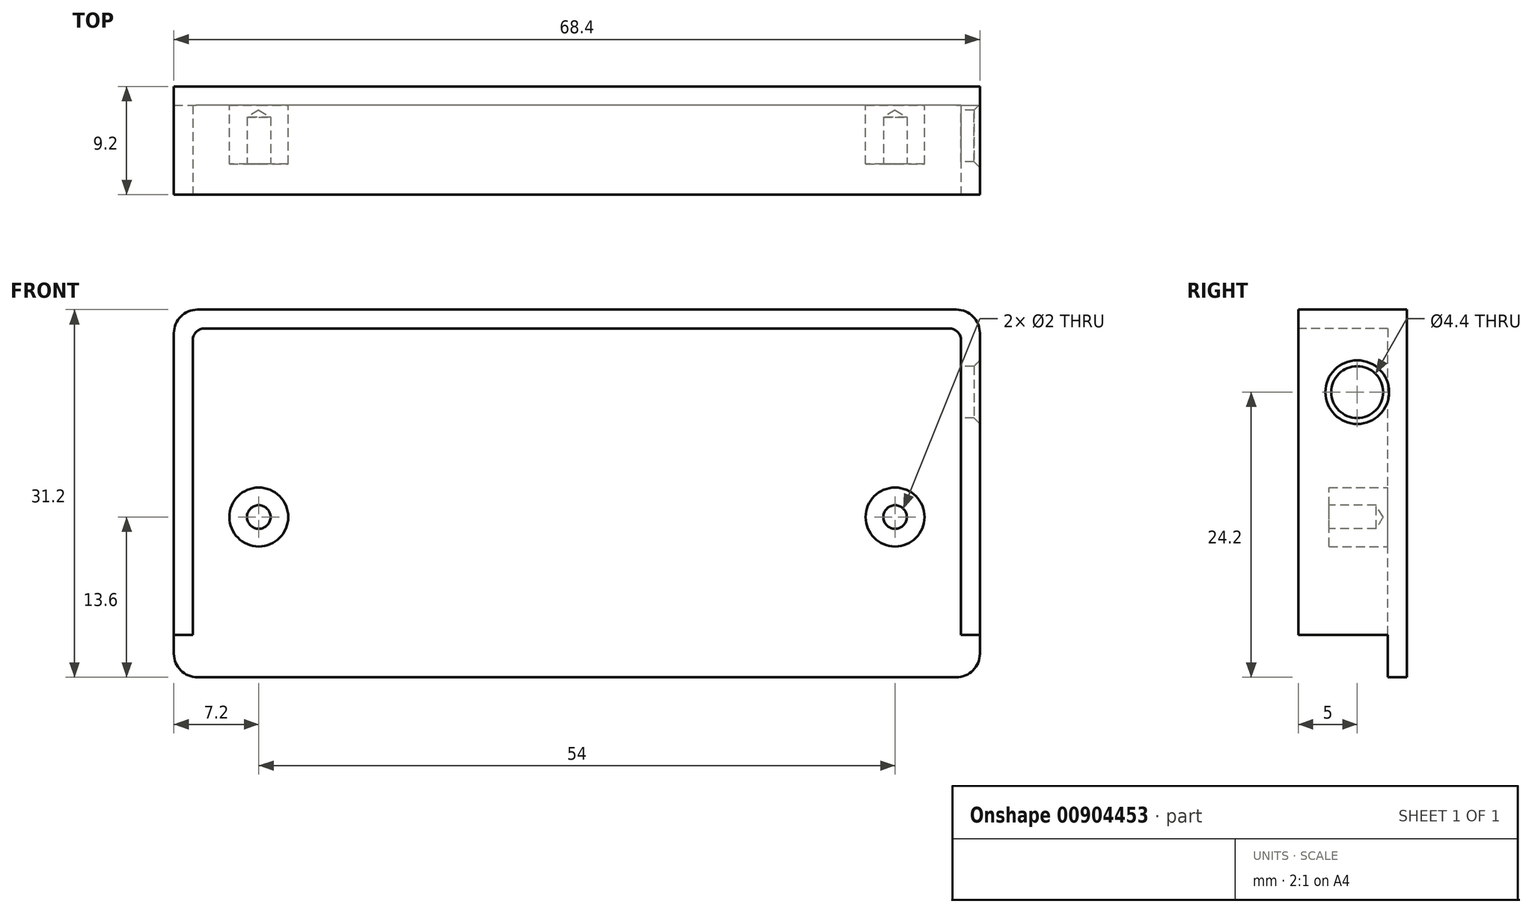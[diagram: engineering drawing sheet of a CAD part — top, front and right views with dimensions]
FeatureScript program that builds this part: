
annotation { "Feature Type Name" : "Feature", "Feature Type Description" : "" }
export const myFeature = defineFeature(function(context is Context, id is Id, definition is map)
    precondition{}
    {
        {
            var Q0;
            Q0=qCreatedBy(makeId("Front.planeOp"),FACE);
            var sketch = newSketch(context, id + "F0", { "sketchPlane" : qUnion([Q0])});
            skLineSegment(sketch, "E0.bottom", {"start": v(34.2, -15.6) * mm, "end": v(-34.2, -15.6) * mm});
            skLineSegment(sketch, "E0.top", {"start": v(34.2, 15.6) * mm, "end": v(-34.2, 15.6) * mm});
            skLineSegment(sketch, "E0.left", {"start": v(34.2, -15.6) * mm, "end": v(34.2, 15.6) * mm});
            skLineSegment(sketch, "E0.right", {"start": v(-34.2, -15.6) * mm, "end": v(-34.2, 15.6) * mm});
            skPoint(sketch, "E0.middle", {"position": v(0, 0) * mm});
            skSolve(sketch);
        }
        {
            var Q0;
            Q0=qSketchRegion(id+"F0",true);
            extrude(context, id + "F1", {"entities" : qUnion([Q0]), "depth" : 9.2 * mm, "offsetDistance" : 25 * mm});
        }
        {
            var Q0;
            Q0=makeQuery(id+"F1.opExtrude","CAP_FACE",FACE,{"disambiguationData":[OSD([sQuery(id+"F0.wireOp",EDGE,"E0.bottom"),sQuery(id+"F0.wireOp",EDGE,"E0.top"),sQuery(id+"F0.wireOp",EDGE,"E0.left"),sQuery(id+"F0.wireOp",EDGE,"E0.right")])],"isStart":false});
            var sketch = newSketch(context, id + "F2", { "sketchPlane" : qUnion([Q0])});
            skLineSegment(sketch, "E1.top", {"start": v(31.6, 14) * mm, "end": v(-31.6, 14) * mm});
            skLineSegment(sketch, "E1.left", {"start": v(32.6, -12) * mm, "end": v(32.6, 13) * mm});
            skLineSegment(sketch, "E1.right", {"start": v(-32.6, -12) * mm, "end": v(-32.6, 13) * mm});
            skPoint(sketch, "E1.middle", {"position": v(0, 1) * mm});
            skCircle(sketch, "E2", {"center": v(-31.6, 13) * mm, "radius": 1 * mm});
            skPoint(sketch, "E2.first.point", {"position": v(-32.6, 13) * mm});
            skPoint(sketch, "E2.second.point", {"position": v(-31.6, 14) * mm});
            skPoint(sketch, "E2.third.point", {"position": v(-30.68, 12.62) * mm});
            skCircle(sketch, "E3", {"center": v(31.6, 13) * mm, "radius": 1 * mm});
            skPoint(sketch, "E3.first.point", {"position": v(32.6, 13) * mm});
            skPoint(sketch, "E3.second.point", {"position": v(31.6, 14) * mm});
            skPoint(sketch, "E3.third.point", {"position": v(30.96, 12.23) * mm});
            skPoint(sketch, "E4.orphan", {"position": v(-32.6, 14) * mm});
            skPoint(sketch, "E5.orphan", {"position": v(32.6, 14) * mm});
            skLineSegment(sketch, "E6.bottom", {"start": v(-34.2, -12) * mm, "end": v(-32.6, -12) * mm});
            skLineSegment(sketch, "E6.top", {"start": v(-34.2, -15.6) * mm, "end": v(34.2, -15.6) * mm});
            skLineSegment(sketch, "E6.left", {"start": v(-34.2, -12) * mm, "end": v(-34.2, -15.6) * mm});
            skLineSegment(sketch, "E6.right", {"start": v(34.2, -12) * mm, "end": v(34.2, -15.6) * mm});
            skLineSegment(sketch, "E7.trimOffspring", {"start": v(32.6, -12) * mm, "end": v(34.2, -12) * mm});
            skSolve(sketch);
        }
        {
            var Q0;
            Q0=qSketchRegion(id+"F2",true);
            extrude(context, id + "F3", {"entities" : qUnion([Q0]), "operationType" : NewBodyOperationType.REMOVE, "oppositeDirection" : true, "depth" : 7.6 * mm, "offsetDistance" : 25 * mm});
        }
        {
            var Q0;
            Q0=makeQuery(id+"F1.opExtrude","SWEPT_EDGE",EDGE,{"disambiguationData":[OSD([sQuery(id+"F0.wireOp",EDGE,"E0.top"),sQuery(id+"F0.wireOp",EDGE,"E0.left")])]});
            fillet(context, id + "F4", {"entities" : qUnion([Q0]), "radius" : 2 * mm, "tangentPropagation" : true, "allowEdgeOverflow" : false});
        }
        {
            var Q0;
            Q0=makeQuery(id+"F1.opExtrude","SWEPT_EDGE",EDGE,{"disambiguationData":[OSD([sQuery(id+"F0.wireOp",EDGE,"E0.top"),sQuery(id+"F0.wireOp",EDGE,"E0.right")])]});
            var Q1;
            Q1=makeQuery(id+"F1.opExtrude","SWEPT_EDGE",EDGE,{"disambiguationData":[OSD([sQuery(id+"F0.wireOp",EDGE,"E0.bottom"),sQuery(id+"F0.wireOp",EDGE,"E0.right")])]});
            fillet(context, id + "F5", {"entities" : qUnion([Q0, Q1]), "radius" : 2 * mm, "tangentPropagation" : true, "allowEdgeOverflow" : false});
        }
        {
            var Q0;
            Q0=makeQuery(id+"F1.opExtrude","SWEPT_EDGE",EDGE,{"disambiguationData":[OSD([sQuery(id+"F0.wireOp",EDGE,"E0.bottom"),sQuery(id+"F0.wireOp",EDGE,"E0.left")])]});
            fillet(context, id + "F6", {"entities" : qUnion([Q0]), "radius" : 2 * mm, "tangentPropagation" : true, "allowEdgeOverflow" : false});
        }
        {
            var Q0;
            Q0=makeQuery(id+"F3.boolean.opBoolean","COPY",FACE,{"derivedFrom":makeQuery(id+"F3.opExtrude","CAP_FACE",FACE,{"disambiguationData":[OSD([sQuery(id+"F2.wireOp",EDGE,"E1.top"),sQuery(id+"F2.wireOp",EDGE,"E1.left"),sQuery(id+"F2.wireOp",EDGE,"E1.right"),sQuery(id+"F2.wireOp",EDGE,"E2"),sQuery(id+"F2.wireOp",EDGE,"E3"),sQuery(id+"F2.wireOp",EDGE,"E6.bottom"),sQuery(id+"F2.wireOp",EDGE,"E6.top"),sQuery(id+"F2.wireOp",EDGE,"E6.left"),sQuery(id+"F2.wireOp",EDGE,"E6.right"),sQuery(id+"F2.wireOp",EDGE,"E7.trimOffspring")])],"isStart":false})});
            var sketch = newSketch(context, id + "F7", { "sketchPlane" : qUnion([Q0])});
            skCircle(sketch, "E8", {"center": v(-27, -2) * mm, "radius": 2.5 * mm});
            skPoint(sketch, "E8.first.point", {"position": v(-29.27, -3.04) * mm});
            skPoint(sketch, "E8.second.point", {"position": v(-26.63, -4.47) * mm});
            skPoint(sketch, "E8.third.point", {"position": v(-27.02, 0.5) * mm});
            skCircle(sketch, "E9", {"center": v(27, -2) * mm, "radius": 2.5 * mm});
            skPoint(sketch, "E9.first.point", {"position": v(26.98, 0.5) * mm});
            skPoint(sketch, "E9.second.point", {"position": v(29.46, -1.55) * mm});
            skPoint(sketch, "E9.third.point", {"position": v(27.02, 0.5) * mm});
            skSolve(sketch);
        }
        {
            var Q0;
            Q0=qSketchRegion(id+"F7",true);
            extrude(context, id + "F8", {"entities" : qUnion([Q0]), "operationType" : NewBodyOperationType.ADD, "depth" : 5 * mm, "offsetDistance" : 25 * mm});
        }
        {
            var Q0;
            Q0=makeQuery(id+"F8.opExtrude","CAP_FACE",FACE,{"disambiguationData":[OSD([sQuery(id+"F7.wireOp",EDGE,"E8")])],"isStart":false});
            var sketch = newSketch(context, id + "F9", { "sketchPlane" : qUnion([Q0])});
            skPoint(sketch, "E10", {"position": v(-27, -2) * mm});
            skSolve(sketch);
        }
        {
            var Q0;
            Q0=sQuery(id+"F9.wireOp",VERTEX,"E10");
            var Q1;
            Q1=makeQuery(id+"F1.opExtrude","SWEPT_BODY",BODY,{"disambiguationData":[OSD([sQuery(id+"F0.wireOp",EDGE,"E0.bottom"),sQuery(id+"F0.wireOp",EDGE,"E0.top"),sQuery(id+"F0.wireOp",EDGE,"E0.left"),sQuery(id+"F0.wireOp",EDGE,"E0.right")])]});
            hole(context, id + "F10", {"style" : HoleStyle.SIMPLE, "endStyle" : HoleEndStyle.BLIND, "holeDiameter" : 2 * mm, "majorDiameter" : 5 * mm, "holeDepth" : 4 * mm, "isTappedThrough" : true, "tappedDepth" : 12 * mm, "tapClearance" : 3, "locations" : qUnion([Q0]), "scope" : qUnion([Q1])});
        }
        {
            var Q0;
            Q0=makeQuery(id+"F8.opExtrude","CAP_FACE",FACE,{"disambiguationData":[OSD([sQuery(id+"F7.wireOp",EDGE,"E9")])],"isStart":false});
            var sketch = newSketch(context, id + "F11", { "sketchPlane" : qUnion([Q0])});
            skPoint(sketch, "E11", {"position": v(27, -2) * mm});
            skSolve(sketch);
        }
        {
            var Q0;
            Q0=sQuery(id+"F11.wireOp",VERTEX,"E11");
            var Q1;
            Q1=makeQuery(id+"F1.opExtrude","SWEPT_BODY",BODY,{"disambiguationData":[OSD([sQuery(id+"F0.wireOp",EDGE,"E0.bottom"),sQuery(id+"F0.wireOp",EDGE,"E0.top"),sQuery(id+"F0.wireOp",EDGE,"E0.left"),sQuery(id+"F0.wireOp",EDGE,"E0.right")])]});
            hole(context, id + "F12", {"style" : HoleStyle.SIMPLE, "endStyle" : HoleEndStyle.BLIND, "holeDiameter" : 2 * mm, "majorDiameter" : 5 * mm, "holeDepth" : 4 * mm, "isTappedThrough" : true, "tappedDepth" : 12 * mm, "tapClearance" : 3, "locations" : qUnion([Q0]), "scope" : qUnion([Q1])});
        }
        {
            var Q0;
            Q0=makeQuery(id+"F3.boolean.opBoolean","COPY",FACE,{"derivedFrom":makeQuery(id+"F3.opExtrude","SWEPT_FACE",FACE,{"disambiguationData":[OSD([sQuery(id+"F2.wireOp",EDGE,"E1.left")])]})});
            var sketch = newSketch(context, id + "F13", { "sketchPlane" : qUnion([Q0])});
            skCircle(sketch, "E12", {"center": v(4.2, 8.6) * mm, "radius": 2.2 * mm});
            skSolve(sketch);
        }
        {
            var Q0;
            Q0=qSketchRegion(id+"F13",true);
            extrude(context, id + "F14", {"entities" : qUnion([Q0]), "operationType" : NewBodyOperationType.REMOVE, "endBound" : BoundingType.THROUGH_ALL, "oppositeDirection" : true, "depth" : 25 * mm, "offsetDistance" : 25 * mm});
        }
        {
            var Q0;
            Q0=makeQuery(id+"F14.boolean.opBoolean","INTERSECT",EDGE,{"derivedFrom":[makeQuery(id+"F1.opExtrude","SWEPT_FACE",FACE,{"disambiguationData":[OSD([sQuery(id+"F0.wireOp",EDGE,"E0.left")])]}),makeQuery(id+"F14.opExtrude","SWEPT_FACE",FACE,{"disambiguationData":[OSD([sQuery(id+"F13.wireOp",EDGE,"E12")])]})]});
            chamfer(context, id + "F15", {"entities" : qUnion([Q0]), "width" : 0.5 * mm, "tangentPropagation" : true});
        }
    });
